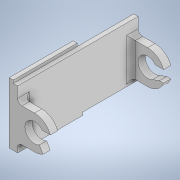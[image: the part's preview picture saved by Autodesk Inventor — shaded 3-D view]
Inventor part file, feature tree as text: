
AUTODESK INVENTOR PART (.ipt)
format: ipt  version: 2020 (Build 240168000, 168)  size: 229,376 bytes
history: native  units: mm
features: extrude x7, sketch x7, projected_geometry x3, fillet x1, plane x1, mirror x1
ambient origin geometry x8: Origin, YZ Plane, XZ Plane, XY Plane, X Axis, Y Axis, Z Axis, Center Point
bodies: Solid1 (feature_tree)
feature tree (20):
  extrude  "Extrusion1"  Depth=83.0mm
  extrude  "Extrusion3"  Depth=42.0mm
  extrude  "Extrusion4"  Depth=44.0mm
  extrude  "Extrusion5"  Depth=38.0mm
  fillet  "Fillet3"  Radius=2.0mm
  plane  "Work Plane1"
  mirror  "Mirror1"
  extrude  "Extrusion6"  Depth=7.5mm TaperAngle=0.0deg
  extrude  "Extrusion7"  Depth=5.0mm
  extrude  "Extrusion8"  Depth=3.0mm
  sketch  "Sketch1"  dims[d0=83.0mm d1=41.5mm]
  sketch  "Sketch3"  dims[d2=42.0mm d3=21.0mm]
  projected_geometry  "Projected Loop1"
  sketch  "Sketch4"  dims[d4=2.85mm d5=0.0mm d12=44.0mm]
  sketch  "Sketch5"  dims[d13=2.0mm d14=38.0mm d15=2.0mm]
  sketch  "Sketch6"  dims[d16=3.0mm d17=0.0mm d18=7.5mm d19=0.0mm]
  projected_geometry  "Projected Loop2"
  sketch  "Sketch7"  dims[d20=13.25mm d21=5.0mm]
  projected_geometry  "Projected Loop3"
  sketch  "Sketch8"  dims[d27=5.0mm d28=0.0mm d29=3.0mm d30=18.0mm d31=4.0mm d32=4.0mm d33=120.0deg d34=13.5mm d35=0.0mm d38=11.5mm d39=0.0mm d40=2.85mm d41=0.0mm d42=120.0deg d43=120.0deg d44=27.925268mm d45=0.872665mm d46=0.5mm d47=0.872665mm]
